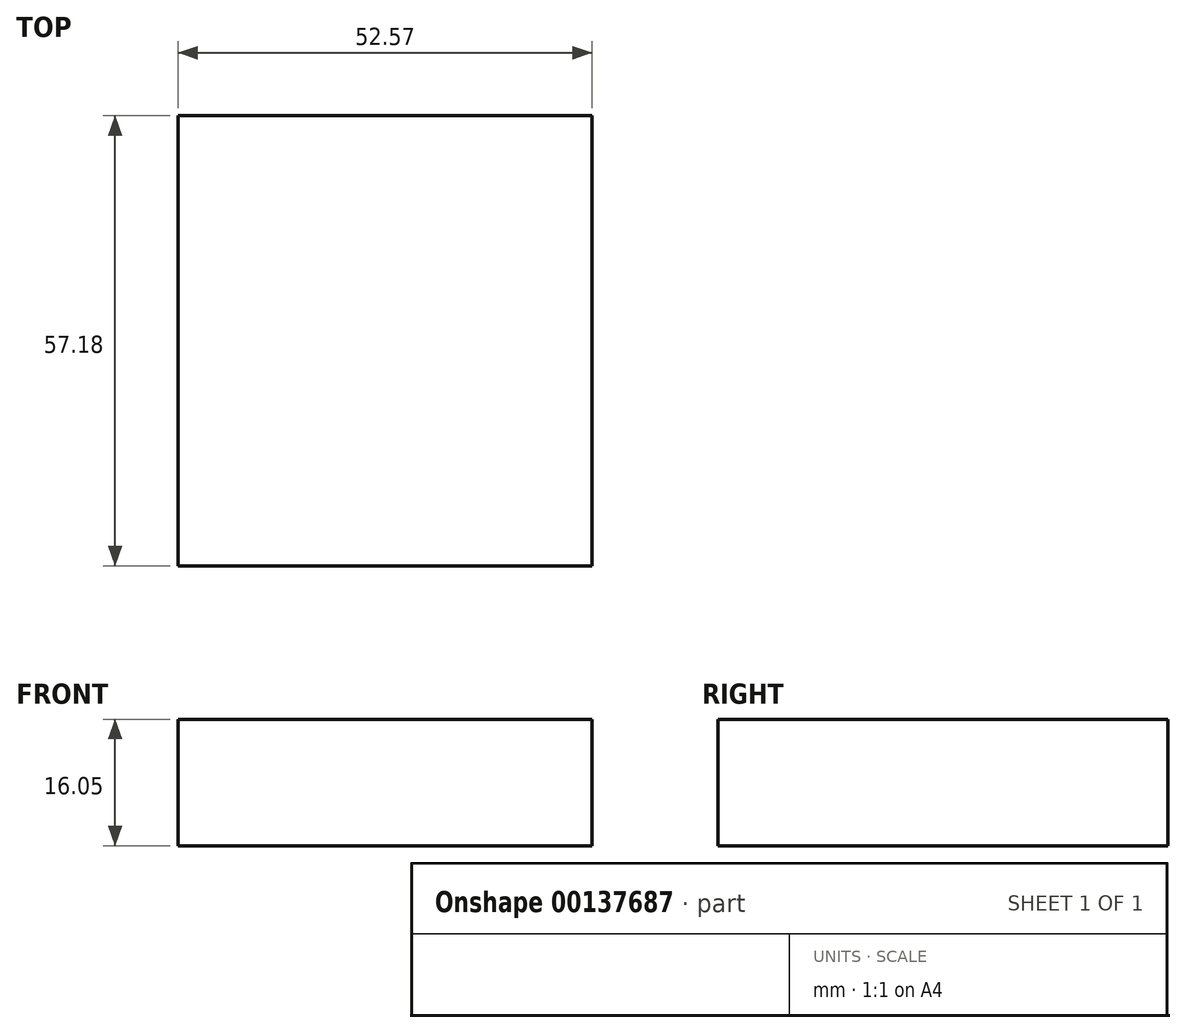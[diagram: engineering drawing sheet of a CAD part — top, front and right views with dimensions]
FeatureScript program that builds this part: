
annotation { "Feature Type Name" : "Feature", "Feature Type Description" : "" }
export const myFeature = defineFeature(function(context is Context, id is Id, definition is map)
    precondition{}
    {
        {
            var Q0;
            Q0=qCreatedBy(makeId("Top.planeOp"),FACE);
            var sketch = newSketch(context, id + "F0", { "sketchPlane" : qUnion([Q0])});
            skLineSegment(sketch, "E0.bottom", {"start": v(-16.71, -20.63) * mm, "end": v(35.86, -20.63) * mm});
            skLineSegment(sketch, "E0.top", {"start": v(-16.71, 36.55) * mm, "end": v(35.86, 36.55) * mm});
            skLineSegment(sketch, "E0.left", {"start": v(-16.71, -20.63) * mm, "end": v(-16.71, 36.55) * mm});
            skLineSegment(sketch, "E0.right", {"start": v(35.86, -20.63) * mm, "end": v(35.86, 36.55) * mm});
            skSolve(sketch);
        }
        {
            var Q0;
            Q0=makeQuery(id+"F0.imprint","IMPRINT",FACE,{"disambiguationData":[TD([[makeQuery(id+"F0.imprint","IMPRINT",EDGE,{"derivedFrom":sQuery(id+"F0.wireOp",EDGE,"E0.bottom")}),1.0]])]});
            extrude(context, id + "F1", {"entities" : qUnion([Q0]), "depth" : 16.05 * mm});
        }
    });
